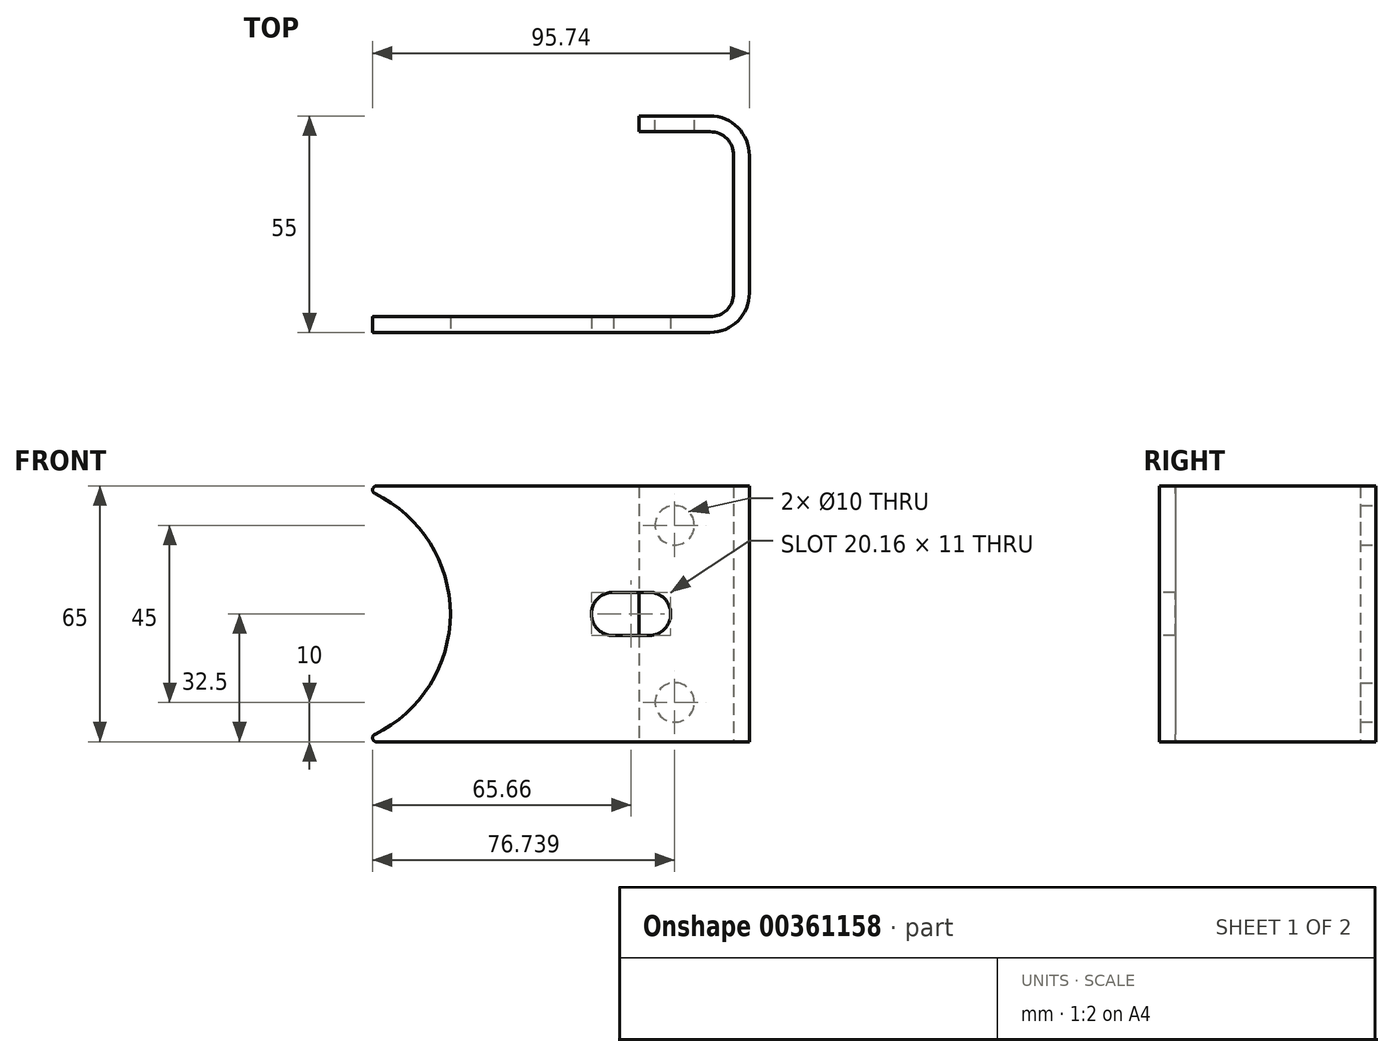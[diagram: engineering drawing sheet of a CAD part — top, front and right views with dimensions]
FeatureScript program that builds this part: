
annotation { "Feature Type Name" : "Feature", "Feature Type Description" : "" }
export const myFeature = defineFeature(function(context is Context, id is Id, definition is map)
    precondition{}
    {
        {
            var Q0;
            Q0=qCreatedBy(makeId("Top.planeOp"),FACE);
            var sketch = newSketch(context, id + "F0", { "sketchPlane" : qUnion([Q0])});
            skLineSegment(sketch, "E0", {"start": v(12.16, 52.98) * mm, "end": v(12.16, 48.98) * mm});
            skLineSegment(sketch, "E1", {"start": v(12.16, 52.98) * mm, "end": v(30.16, 52.98) * mm});
            skLineSegment(sketch, "E2", {"start": v(40.16, 42.98) * mm, "end": v(40.16, 7.98) * mm});
            skLineSegment(sketch, "E3", {"start": v(12.16, 48.98) * mm, "end": v(30.16, 48.98) * mm});
            skLineSegment(sketch, "E4", {"start": v(36.16, 42.98) * mm, "end": v(36.16, 7.98) * mm});
            skPoint(sketch, "E5.visualSharp", {"position": v(40.16, 52.98) * mm});
            skArc(sketch, "E5.filletArc", {"start": v(40.16, 42.98) * mm, "mid": v(37.23, 50.05) * mm, "end": v(30.16, 52.98) * mm});
            skPoint(sketch, "E6.visualSharp", {"position": v(36.16, 48.98) * mm});
            skArc(sketch, "E6.filletArc", {"start": v(36.16, 42.98) * mm, "mid": v(34.4, 47.22) * mm, "end": v(30.16, 48.98) * mm});
            skLineSegment(sketch, "E7", {"start": v(30.16, -2.02) * mm, "end": v(-59.85, -2.02) * mm});
            skLineSegment(sketch, "E8", {"start": v(-59.85, -2.02) * mm, "end": v(-59.85, 1.98) * mm});
            skLineSegment(sketch, "E9", {"start": v(-59.85, 1.98) * mm, "end": v(30.16, 1.98) * mm});
            skPoint(sketch, "E10.visualSharp", {"position": v(40.16, -2.02) * mm});
            skArc(sketch, "E10.filletArc", {"start": v(30.16, -2.02) * mm, "mid": v(37.23, 0.9) * mm, "end": v(40.16, 7.98) * mm});
            skPoint(sketch, "E11.visualSharp", {"position": v(36.16, 1.98) * mm});
            skArc(sketch, "E11.filletArc", {"start": v(30.16, 1.98) * mm, "mid": v(34.4, 3.74) * mm, "end": v(36.16, 7.98) * mm});
            skSolve(sketch);
        }
        {
            var Q0;
            Q0 = qSketchRegion(id + "F0", true);
            extrude(context, id + "F1", {"entities" : qUnion([Q0]), "depth" : 65 * mm});
        }
        {
            var Q0;
            Q0=makeQuery(id+"F1.opExtrude","SWEPT_FACE",FACE,{"disambiguationData":[OSD([sQuery(id+"F0.wireOp",EDGE,"E1")])]});
            var sketch = newSketch(context, id + "F2", { "sketchPlane" : qUnion([Q0])});
            skCircle(sketch, "E12", {"center": v(-21.16, 10) * mm, "radius": 5 * mm});
            skCircle(sketch, "E13", {"center": v(-21.16, 55) * mm, "radius": 5 * mm});
            skPoint(sketch, "E14.end.orphan", {"position": v(-12.16, 10) * mm});
            skPoint(sketch, "E15.end.orphan", {"position": v(-21.16, 0) * mm});
            skSolve(sketch);
        }
        {
            var Q0;
            Q0 = qSketchRegion(id + "F2", true);
            extrude(context, id + "F3", {"entities" : qUnion([Q0]), "operationType" : NewBodyOperationType.REMOVE, "oppositeDirection" : true, "depth" : 25 * mm});
        }
        {
            var Q0;
            Q0=makeQuery(id+"F1.opExtrude","SWEPT_FACE",FACE,{"disambiguationData":[OSD([sQuery(id+"F0.wireOp",EDGE,"E7")])]});
            var sketch = newSketch(context, id + "F4", { "sketchPlane" : qUnion([Q0])});
            skArc(sketch, "E16", {"start": v(-59.85, 0) * mm, "mid": v(-35.84, 32.5) * mm, "end": v(-59.85, 65) * mm});
            skLineSegment(sketch, "E17", {"start": v(-59.85, 65) * mm, "end": v(-59.85, 0) * mm});
            skSolve(sketch);
        }
        {
            var Q0;
            Q0 = qSketchRegion(id + "F4", true);
            extrude(context, id + "F5", {"entities" : qUnion([Q0]), "operationType" : NewBodyOperationType.REMOVE, "oppositeDirection" : true, "depth" : 25 * mm});
        }
        {
            var Q0;
            {var subQ0=sQuery(id+"F4.wireOp",EDGE,"E17");var subQ1=sQuery(id+"F4.wireOp",EDGE,"E16");var subQ2=sQuery(id+"F0.wireOp",EDGE,"E7");Q0=makeQuery(id+"F5.boolean.opBoolean","MERGE",EDGE,{"derivedFrom":[makeQuery(id+"F1.opExtrude","CAP_EDGE",EDGE,{"disambiguationData":[OSD([sQuery(id+"F0.wireOp",EDGE,"E8")])],"isStart":false}),makeQuery(id+"F5.opExtrude","SWEPT_EDGE",EDGE,{"disambiguationData":[OSD([subQ2,subQ1,subQ0]),TDD([makeQuery(id+"F4.imprint","INTERSECT",VERTEX,{"derivedFrom":[makeQuery(id+"F1.opExtrude","CAP_EDGE",EDGE,{"disambiguationData":[OSD([subQ2])],"isStart":false}),subQ1,subQ0]})])]})]});}
            var Q1;
            {var subQ0=sQuery(id+"F4.wireOp",EDGE,"E17");var subQ1=sQuery(id+"F4.wireOp",EDGE,"E16");var subQ2=sQuery(id+"F0.wireOp",EDGE,"E7");Q1=makeQuery(id+"F5.boolean.opBoolean","MERGE",EDGE,{"derivedFrom":[makeQuery(id+"F1.opExtrude","CAP_EDGE",EDGE,{"disambiguationData":[OSD([sQuery(id+"F0.wireOp",EDGE,"E8")])],"isStart":true}),makeQuery(id+"F5.opExtrude","SWEPT_EDGE",EDGE,{"disambiguationData":[OSD([subQ2,subQ1,subQ0]),TDD([makeQuery(id+"F4.imprint","INTERSECT",VERTEX,{"derivedFrom":[makeQuery(id+"F1.opExtrude","CAP_EDGE",EDGE,{"disambiguationData":[OSD([subQ2])],"isStart":true}),subQ1,subQ0]})])]})]});}
            fillet(context, id + "F6", {"entities" : qUnion([Q0, Q1]), "radius" : 1 * mm, "tangentPropagation" : true, "allowEdgeOverflow" : false});
        }
        {
            var Q0;
            Q0=makeQuery(id+"F1.opExtrude","SWEPT_FACE",FACE,{"disambiguationData":[OSD([sQuery(id+"F0.wireOp",EDGE,"E7")])]});
            var sketch = newSketch(context, id + "F7", { "sketchPlane" : qUnion([Q0])});
            skPoint(sketch, "E18.orphan", {"position": v(30.16, 32.5) * mm});
            skPoint(sketch, "E19.start.orphan", {"position": v(-35.84, 32.5) * mm});
            skLineSegment(sketch, "E20", {"start": v(14.66, 38) * mm, "end": v(5.66, 38) * mm});
            skLineSegment(sketch, "E21", {"start": v(10.16, 27) * mm, "end": v(5.66, 27) * mm});
            skLineSegment(sketch, "E22", {"start": v(10.16, 27) * mm, "end": v(14.66, 27) * mm});
            skArc(sketch, "E23", {"start": v(5.66, 38) * mm, "mid": v(0, 32.5) * mm, "end": v(5.66, 27) * mm});
            skArc(sketch, "E24", {"start": v(14.66, 27) * mm, "mid": v(20.16, 32.5) * mm, "end": v(14.66, 38) * mm});
            skPoint(sketch, "E25.start.orphan", {"position": v(20.16, 32.5) * mm});
            skSolve(sketch);
        }
        {
            var Q0;
            Q0 = qSketchRegion(id + "F7", true);
            extrude(context, id + "F8", {"entities" : qUnion([Q0]), "operationType" : NewBodyOperationType.REMOVE, "oppositeDirection" : true, "depth" : 15 * mm});
        }
    });
